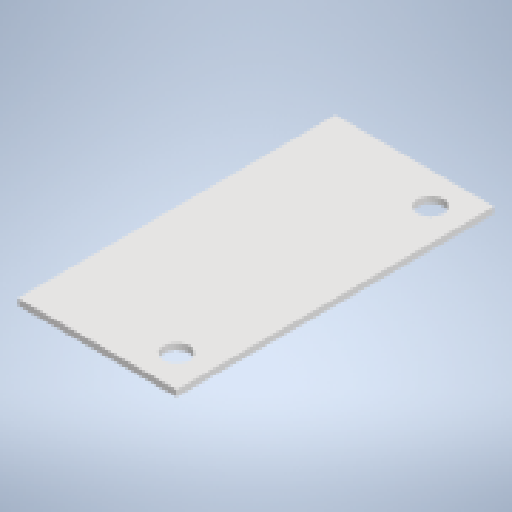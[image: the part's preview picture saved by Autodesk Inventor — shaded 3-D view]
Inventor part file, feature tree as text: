
AUTODESK INVENTOR PART (.ipt)
format: ipt  version: 2023 (Build 270158000, 158)  size: 218,112 bytes
history: native  units: mm
features: extrude x1, sketch x1
ambient origin geometry x8: Origin, YZ Plane, XZ Plane, XY Plane, X Axis, Y Axis, Z Axis, Center Point
bodies: Body1 (feature_tree)
feature tree (2):
  extrude  "Extrusion2"  Depth=100.0mm
  sketch  "Sketch1"  dims[d0=50.0mm d1=100.0mm d8=10.0mm d9=10.0mm d10=8.0mm d11=10.0mm d12=10.0mm d13=8.0mm d14=2.0mm d15=0.0mm]
